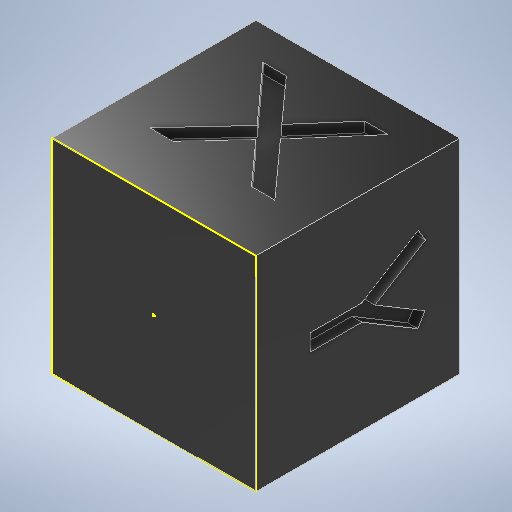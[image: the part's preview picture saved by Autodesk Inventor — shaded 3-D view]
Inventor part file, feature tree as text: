
AUTODESK INVENTOR PART (.ipt)
format: ipt  version: 2025.2 (Build 292293000, 293)  size: 587,264 bytes
history: native  units: in
note: dims shown in document units (in); Inventor stores cm internally (conversion verified against a paired STEP export)
features: sketch x5, extrude x4, projected_geometry x1
ambient origin geometry x8: Origin, YZ Plane, XZ Plane, XY Plane, X Axis, Y Axis, Z Axis, Center Point
bodies: Solid1 (feature_tree)
feature tree (10):
  extrude  "Extrusion1"  Depth=0.7874in
  sketch  "Sketch2"  dims[d2=0.0in d5=0.0394in d6=0.0in]
  extrude  "Extrusion2"  Depth=0.0394in TaperAngle=0.0deg
  extrude  "Extrusion3"  Depth=0.0394in TaperAngle=0.0deg
  extrude  "Extrusion4"  Depth=0.0344in
  sketch  "Sketch1"  dims[d0=0.7874in d1=0.7874in]
  projected_geometry  "Projected Loop1"
  sketch  "Sketch3"  dims[d7=0.0394in d8=0.0in d9=0.0394in d10=0.0in]
  sketch  "Sketch4"  dims[d11=0.0197in d12=0.0344in]
  sketch  "Sketch5"  dims[d13=0.0197in d14=0.0344in]
